# Revit family: PVC1149_12inch DCB PVC Waterstop
name_source: partatom
category: Specialty Equipment
units: mm (PartAtom-declared; Revit-internal decimal feet)

## family parameters
Cut with Voids When Loaded = No
OmniClass Number = 23.10.00.00
OmniClass Title = Site Products
Part Type = Normal
Room Calculation Point = No
Round Connector Dimension = Use Diameter
Shared = No
Work Plane-Based = No

## types (2) — shared parameters
Assembly Code = F1030
Certifications = NSF 61, NSF 372, CRD C-572-74, ASTM D567
Description = PVC1149 is 12" x 3/8" x 50' Earth Shield PVC dumbbell centerbulb waterstop.
Edition number = 1
Height = 1.5 "
Hydrophilic = No
Hydrophobic = Yes
Keynote = 13000
Manufacturer = J P Specialties Inc.
Materials = PVC
Model = PVC1149
Product Guid = 27e5cdcc-cece-4d8c-947d-ca6b8ef269ba
Product Material = JP Specialties - Polyvinyl Chloride (PVC)
Product data url = www.bimmodeller.com/jpspecialties/products/Polyvinyl-Chloride-PVC-Waterstop
Telephone = 951-763-7077
URL = https://www.jpspecialties.com
Weight = 3.9 lbs/lft
Width = 11.88 "

## per-type parameters (varying)
| type | z_Horizontal | z_Vertical |
| PVC1149 - Horizontal | Yes | No |
| PVC1149 - Vertical | No | Yes |

## geometry (parser evidence)
native form markers: Sweep x4
no freeform markers — native parametric forms only
